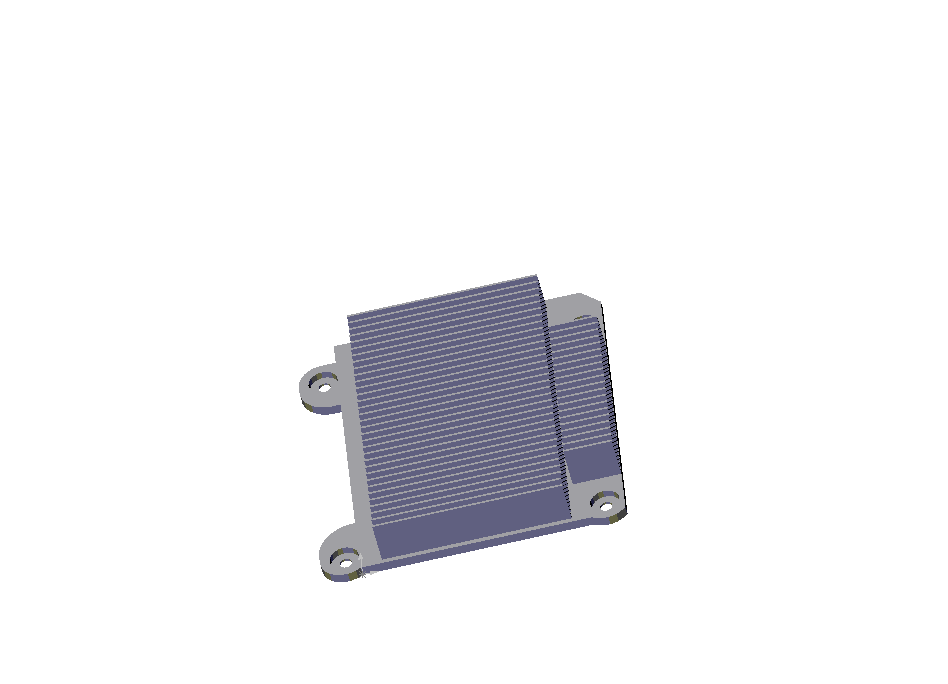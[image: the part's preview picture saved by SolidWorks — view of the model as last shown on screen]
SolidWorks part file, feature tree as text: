
SOLIDWORKS PART (.sldprt)
format: sldprt  version: not decoded by parser v0  size: 321,024 bytes
history: native  units: mm
features: sketch x5, plane x3, extrude x3, cut_extrude x2 (+5 scaffold rows collapsed)
feature tree (18):
  scaffold x5  (default folders/planes/origin — collapsed)
  plane  "Plan1"
  plane  "Plan2"
  plane  "Plan3"
  sketch  "Esquisse1"  dims[c1.D3=2.0mm c1.D5=10.0mm c1.D7=10.0mm c1.D9=4.0mm c2.D5=10.0mm c2.D1=54.5mm c2.D2=67.5mm c2.D3=57.5mm c2.D4=10.0mm c3.D5=53.5mm c3.D6=57.5mm c3.D7=4.0mm c3.D8=63.5mm c3.D9=~2.462011mm c4.D5=53.5mm c4.D6=53.5mm c4.D9=4.0mm c4.D10=4.0mm c5.D9=~80.655893deg]
  extrude  "Base-Extrusion"  Depth=2mm
  sketch  "Esquisse2"  dims[c1.D1=~14.142136mm c1.D3=10.0mm c1.D5=10.0mm c1.D7=10.0mm c2.D1=57.5mm c2.D2=10.0mm c2.D3=53.5mm c2.D4=57.5mm c2.D5=10.0mm c2.D6=4.0mm c2.D7=4.0mm c2.D8=53.5mm]
  cut_extrude  "Enlèv. mat.-Extru.1"  Depth=1.5mm
  sketch  "Esquisse3"  dims[c1.D1=10.0mm c1.D3=~14.142136mm c1.D5=10.0mm c1.D7=10.0mm c2.D1=10.0mm c2.D2=57.5mm c2.D3=4.0mm c2.D4=10.0mm c2.D5=4.0mm c2.D6=53.5mm c2.D7=53.5mm c2.D8=53.5mm]
  cut_extrude  "Enlèv. mat.-Extru.2"  [1 undecoded]
  sketch  "Esquisse4"  dims[D1=0.5mm D2=39.0mm D3=4.5mm D4=1.0mm D5=39.0mm D6=0.5mm D7=1.5mm D8=4.5mm D9=0.5mm D10=1.5mm D11=0.5mm D12=1.5mm D13=1.5mm D14=0.5mm D15=0.5mm D16=1.5mm D17=1.0mm D18=1.5mm D19=0.5mm D20=10.0mm D21=39.0mm D22=4.5mm D23=0.5mm D24=1.5mm D25=1.5mm D26=0.5mm D27=1.5mm D28=0.5mm D29=1.5mm D30=0.5mm D31=1.5mm D32=0.5mm D33=1.5mm D34=0.5mm D35=1.5mm D36=0.5mm D37=1.5mm D38=0.5mm D39=1.5mm D40=0.5mm D41=1.5mm D42=0.5mm]
  extrude  "Boss.-Extru.2"  Depth=9mm
  sketch  "Esquisse5"  dims[c1.D1=39.0mm c1.D2=1.5mm c1.D3=11.0mm c1.D4=0.5mm c1.D5=10.0mm c1.D6=1.5mm c1.D7=1.0mm c1.D8=0.5mm c2.D7=1.0mm c2.D9=1.5mm c2.D10=0.5mm c2.D11=1.5mm c2.D12=0.5mm c2.D13=1.5mm c2.D14=0.5mm c2.D15=1.5mm c2.D16=0.5mm c2.D17=1.5mm c2.D18=0.5mm c2.D19=1.5mm c2.D20=0.5mm c2.D21=1.5mm c2.D22=0.5mm c2.D23=1.5mm c2.D24=1.5mm c2.D25=1.5mm c2.D26=1.5mm c2.D27=1.5mm c2.D28=1.5mm c2.D29=1.5mm c2.D30=1.5mm c2.D31=1.5mm c2.D32=0.5mm c2.D33=0.5mm c2.D34=0.5mm c2.D35=0.5mm c2.D36=0.5mm c2.D37=0.5mm c2.D38=~1.726278mm c3.D38=90.0deg c4.D38=0.5mm c4.D39=0.5mm c4.D40=0.5mm c4.D41=1.5mm c4.D42=0.5mm c4.D43=1.5mm c4.D44=~0.909012mm c5.D44=90.0deg c6.D44=0.5mm c6.D45=0.5mm c6.D46=1.5mm c6.D47=1.5mm c6.D48=0.5mm c6.D49=1.5mm c6.D50=0.5mm c6.D51=1.5mm c6.D52=0.5mm c6.D53=1.5mm c6.D54=0.5mm c6.D55=1.5mm c6.D56=0.5mm c6.D57=2.0mm c6.D58=2.0mm]
  extrude  "Boss.-Extru.3"  Depth=9mm
decode coverage: 9 of 10 modeling features carry decoded parameters
note: ~ marks probable driven/reference dimensions
note: 1 parameter value undecoded
note: suppression state not decoded; provenance and decode notes live in map.json
